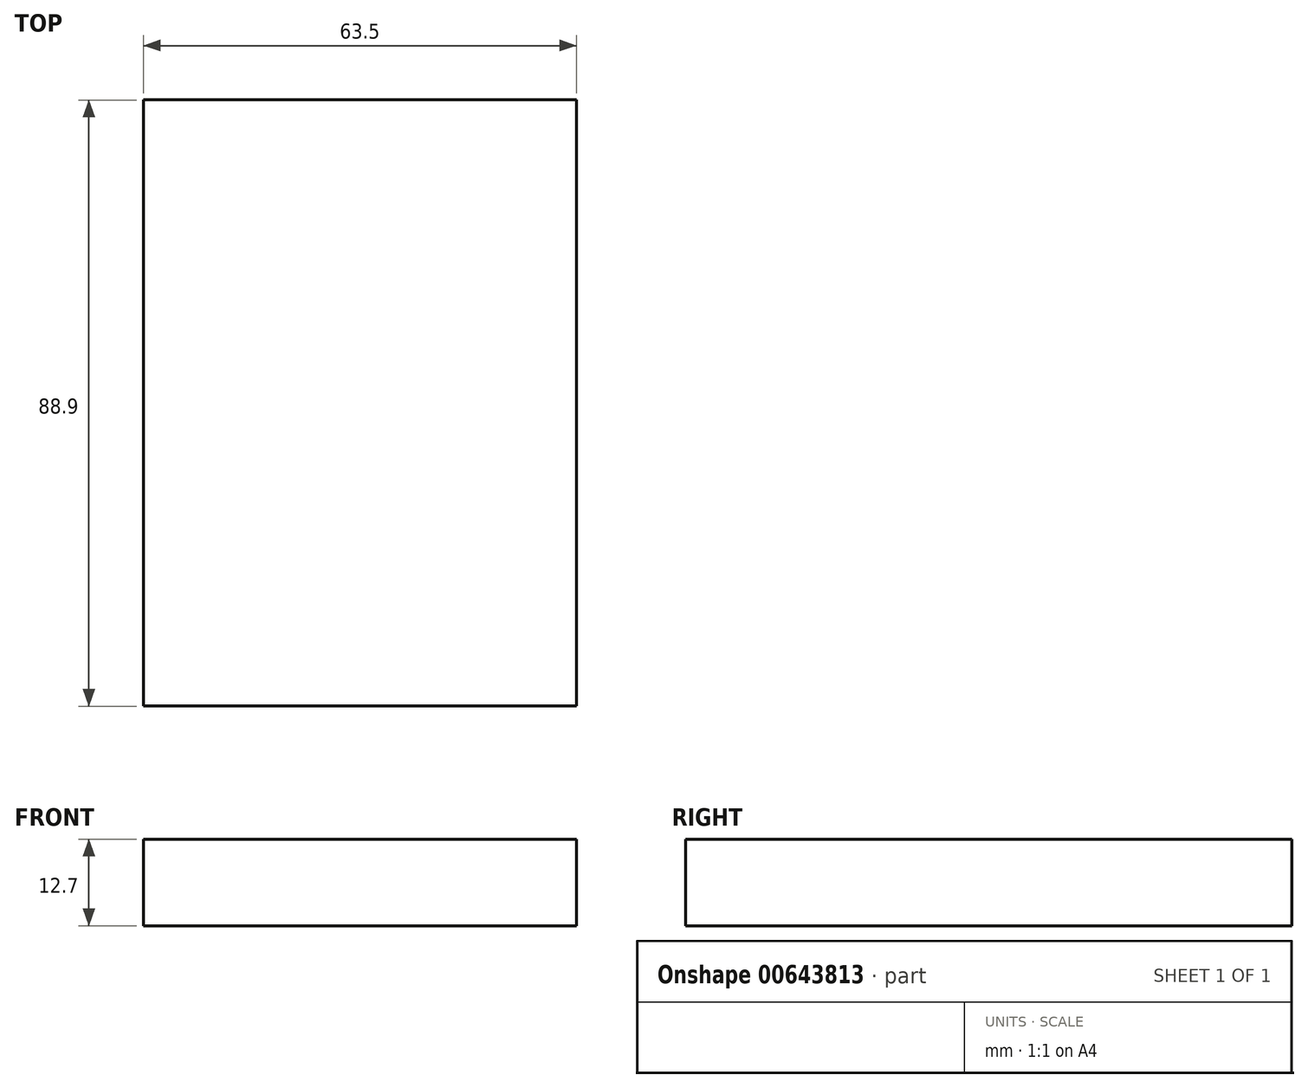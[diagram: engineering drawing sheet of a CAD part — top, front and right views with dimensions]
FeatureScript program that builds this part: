
annotation { "Feature Type Name" : "Feature", "Feature Type Description" : "" }
export const myFeature = defineFeature(function(context is Context, id is Id, definition is map)
    precondition{}
    {
        {
            var Q0;
            Q0=qCreatedBy(makeId("Top.planeOp"),FACE);
            var sketch = newSketch(context, id + "F0", { "sketchPlane" : qUnion([Q0])});
            skLineSegment(sketch, "E0.bottom", {"start": v(-31.34, 47.96) * mm, "end": v(32.16, 47.96) * mm});
            skLineSegment(sketch, "E0.top", {"start": v(-31.34, -40.94) * mm, "end": v(32.16, -40.94) * mm});
            skLineSegment(sketch, "E0.left", {"start": v(-31.34, 47.96) * mm, "end": v(-31.34, -40.94) * mm});
            skLineSegment(sketch, "E0.right", {"start": v(32.16, 47.96) * mm, "end": v(32.16, -40.94) * mm});
            skSolve(sketch);
        }
        {
            var Q0;
            Q0 = qSketchRegion(id + "F0", true);
            extrude(context, id + "F1", {"entities" : qUnion([Q0]), "depth" : 12.7 * mm, "offsetDistance" : 25.4 * mm});
        }
    });
